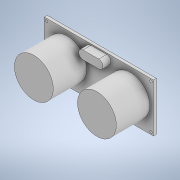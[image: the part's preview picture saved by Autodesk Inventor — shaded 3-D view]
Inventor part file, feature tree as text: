
AUTODESK INVENTOR PART (.ipt)
format: ipt  version: 2020 (Build 240168000, 168)  size: 269,312 bytes
history: native  units: mm
features: extrude x8, sketch x8, other x2, fillet x1, projected_geometry x1
ambient origin geometry x8: Origin, YZ Plane, XZ Plane, XY Plane, X Axis, Y Axis, Z Axis, Center Point
bodies: Body1 (feature_tree)
feature tree (20):
  other  "Ultrasonic HC-SRO4"
  other  "Твердое тело1"
  extrude  "Выдавливание1"  Depth=45.0mm
  extrude  "Выдавливание2"  Depth=20.0mm
  extrude  "Выдавливание3"  Depth=1.2mm TaperAngle=0.0deg
  extrude  "Выдавливание8"  Depth=1.5mm
  extrude  "Выдавливание4"  Depth=16.0mm
  extrude  "Выдавливание5"  Depth=13.8mm TaperAngle=0.0deg
  extrude  "Выдавливание6"  Depth=0.5mm
  extrude  "Выдавливание7"  Depth=10.0mm
  fillet  "Сопряжение1"  Radius=3.5mm
  sketch  "Эскиз1"
  sketch  "Эскиз2"
  sketch  "Эскиз3"
  sketch  "Эскиз4"
  sketch  "Эскиз5"
  sketch  "Эскиз6"
  sketch  "Эскиз7"
  projected_geometry  "Спроецированная петля1"
  sketch  "Эскиз8"
